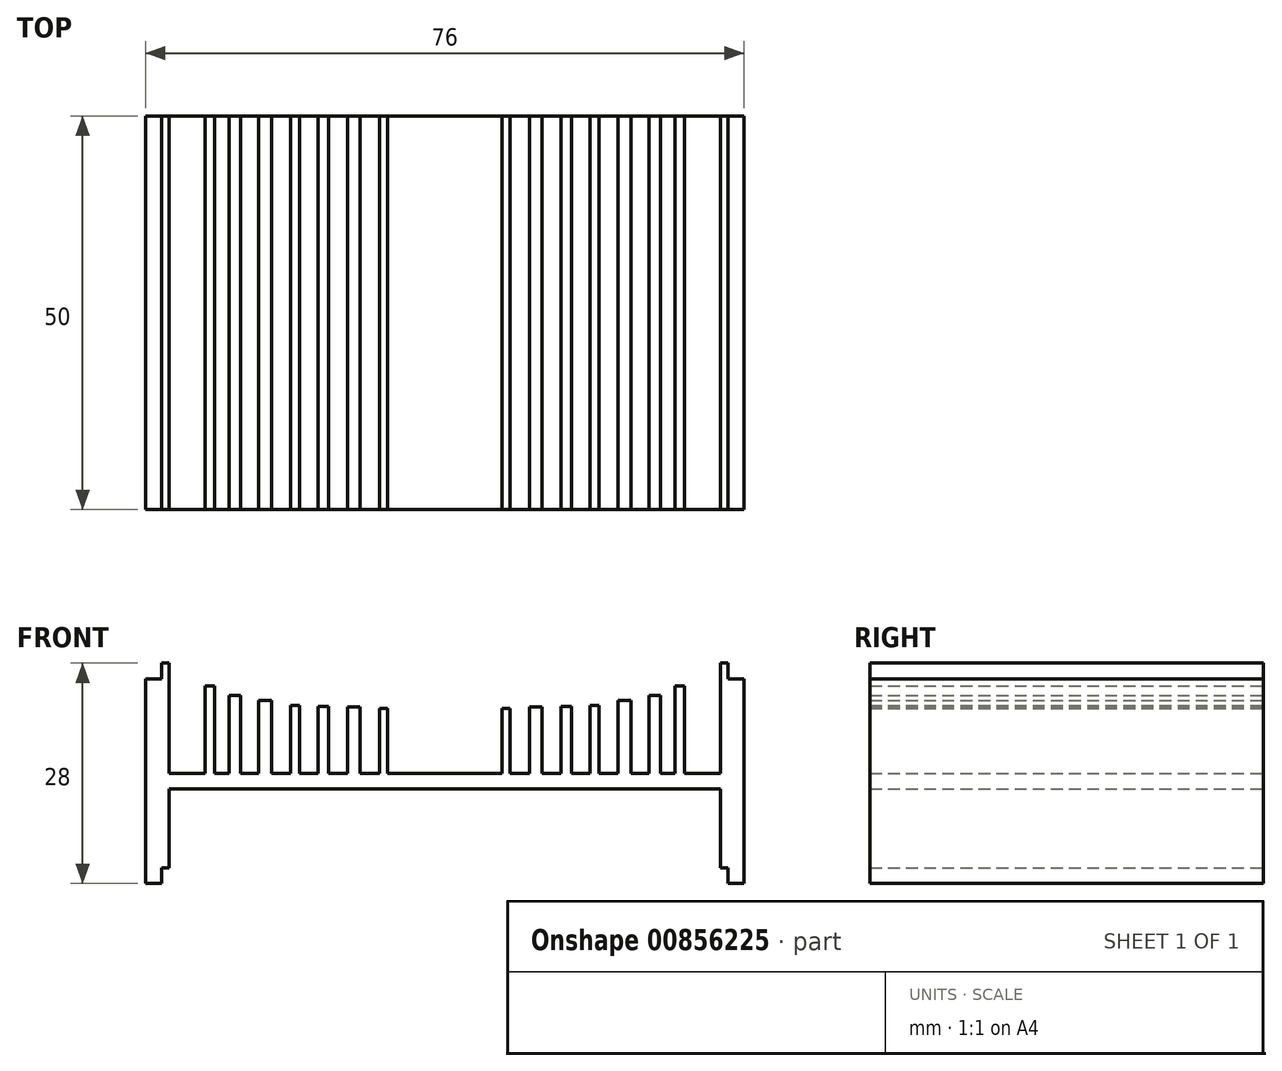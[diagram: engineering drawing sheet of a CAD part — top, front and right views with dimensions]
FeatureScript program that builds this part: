
annotation { "Feature Type Name" : "Feature", "Feature Type Description" : "" }
export const myFeature = defineFeature(function(context is Context, id is Id, definition is map)
    precondition{}
    {
        {
            var Q0;
            Q0=qCreatedBy(makeId("Front.planeOp"),FACE);
            var sketch = newSketch(context, id + "F0", { "sketchPlane" : qUnion([Q0])});
            skLineSegment(sketch, "E0", {"start": v(-34.72, -1.16) * mm, "end": v(-34.72, -27.16) * mm});
            skLineSegment(sketch, "E1", {"start": v(-34.72, -27.16) * mm, "end": v(-32.72, -27.16) * mm});
            skLineSegment(sketch, "E2", {"start": v(-32.72, -27.16) * mm, "end": v(-32.72, -25.16) * mm});
            skLineSegment(sketch, "E3", {"start": v(-32.72, -25.16) * mm, "end": v(-31.72, -25.16) * mm});
            skLineSegment(sketch, "E4", {"start": v(-31.72, -25.16) * mm, "end": v(-31.72, -15.16) * mm});
            skLineSegment(sketch, "E5", {"start": v(-31.72, -15.16) * mm, "end": v(3.28, -15.16) * mm});
            skLineSegment(sketch, "E6", {"start": v(-34.72, -1.16) * mm, "end": v(-32.72, -1.16) * mm});
            skLineSegment(sketch, "E7", {"start": v(-32.72, -1.16) * mm, "end": v(-32.72, 0.84) * mm});
            skLineSegment(sketch, "E8", {"start": v(-32.72, 0.84) * mm, "end": v(-31.72, 0.84) * mm});
            skLineSegment(sketch, "E9", {"start": v(-31.72, 0.84) * mm, "end": v(-31.72, -13.16) * mm});
            skLineSegment(sketch, "E10", {"start": v(-31.72, -13.16) * mm, "end": v(-27.2, -13.16) * mm});
            skLineSegment(sketch, "E11", {"start": v(3.28, -13.16) * mm, "end": v(3.28, -15.16) * mm});
            skLineSegment(sketch, "E12", {"start": v(3.28, 2.27) * mm, "end": v(3.28, -31.1) * mm, "construction": true});
            skLineSegment(sketch, "E13.MirrorCS", {"start": v(41.28, -1.16) * mm, "end": v(41.28, -27.16) * mm});
            skLineSegment(sketch, "E14.MirrorCS", {"start": v(38.28, 0.84) * mm, "end": v(38.28, -13.16) * mm});
            skLineSegment(sketch, "E15.MirrorCS", {"start": v(41.28, -1.16) * mm, "end": v(39.28, -1.16) * mm});
            skLineSegment(sketch, "E16.MirrorCS", {"start": v(39.28, -1.16) * mm, "end": v(39.28, 0.84) * mm});
            skLineSegment(sketch, "E17.MirrorCS", {"start": v(39.28, 0.84) * mm, "end": v(38.28, 0.84) * mm});
            skLineSegment(sketch, "E18.MirrorCS", {"start": v(38.28, -13.16) * mm, "end": v(33.75, -13.16) * mm});
            skLineSegment(sketch, "E19.MirrorCS", {"start": v(38.28, -15.16) * mm, "end": v(3.28, -15.16) * mm});
            skLineSegment(sketch, "E20.MirrorCS", {"start": v(38.28, -25.16) * mm, "end": v(38.28, -15.16) * mm});
            skLineSegment(sketch, "E21.MirrorCS", {"start": v(39.28, -25.16) * mm, "end": v(38.28, -25.16) * mm});
            skLineSegment(sketch, "E22.MirrorCS", {"start": v(41.28, -27.16) * mm, "end": v(39.28, -27.16) * mm});
            skLineSegment(sketch, "E23.MirrorCS", {"start": v(39.28, -27.16) * mm, "end": v(39.28, -25.16) * mm});
            skLineSegment(sketch, "E24", {"start": v(-27.2, -13.16) * mm, "end": v(-27.2, -2.1) * mm});
            skLineSegment(sketch, "E25", {"start": v(-27.2, -2.1) * mm, "end": v(-25.98, -2.1) * mm});
            skLineSegment(sketch, "E26", {"start": v(-25.98, -2.1) * mm, "end": v(-25.98, -13.16) * mm});
            skLineSegment(sketch, "E27.trimOffspring", {"start": v(-25.98, -13.16) * mm, "end": v(-24.09, -13.16) * mm});
            skLineSegment(sketch, "E28", {"start": v(-24.09, -13.16) * mm, "end": v(-24.09, -3.29) * mm});
            skLineSegment(sketch, "E29", {"start": v(-24.09, -3.29) * mm, "end": v(-22.68, -3.29) * mm});
            skLineSegment(sketch, "E30", {"start": v(-22.68, -3.29) * mm, "end": v(-22.68, -13.16) * mm});
            skLineSegment(sketch, "E31", {"start": v(-22.68, -13.16) * mm, "end": v(-20.35, -13.16) * mm});
            skLineSegment(sketch, "E32", {"start": v(-20.35, -13.16) * mm, "end": v(-20.35, -3.9) * mm});
            skLineSegment(sketch, "E33", {"start": v(-20.35, -3.9) * mm, "end": v(-18.7, -3.9) * mm});
            skLineSegment(sketch, "E34", {"start": v(-18.7, -3.9) * mm, "end": v(-18.7, -13.16) * mm});
            skLineSegment(sketch, "E35", {"start": v(-18.7, -13.16) * mm, "end": v(-16.3, -13.16) * mm});
            skLineSegment(sketch, "E36", {"start": v(-16.3, -13.16) * mm, "end": v(-16.3, -4.5) * mm});
            skLineSegment(sketch, "E37", {"start": v(-16.3, -4.5) * mm, "end": v(-15.14, -4.5) * mm});
            skLineSegment(sketch, "E38", {"start": v(-15.14, -4.5) * mm, "end": v(-15.14, -13.16) * mm});
            skLineSegment(sketch, "E39", {"start": v(-15.14, -13.16) * mm, "end": v(-12.81, -13.16) * mm});
            skLineSegment(sketch, "E40", {"start": v(-12.81, -13.16) * mm, "end": v(-12.81, -4.69) * mm});
            skLineSegment(sketch, "E41", {"start": v(-12.81, -4.69) * mm, "end": v(-11.47, -4.69) * mm});
            skLineSegment(sketch, "E42", {"start": v(-11.47, -4.69) * mm, "end": v(-11.47, -13.16) * mm});
            skLineSegment(sketch, "E43", {"start": v(-9.08, -13.16) * mm, "end": v(-9.08, -4.75) * mm});
            skLineSegment(sketch, "E44", {"start": v(-9.08, -4.75) * mm, "end": v(-7.48, -4.75) * mm});
            skLineSegment(sketch, "E45", {"start": v(-7.48, -4.75) * mm, "end": v(-7.48, -13.16) * mm});
            skLineSegment(sketch, "E46", {"start": v(-7.48, -13.16) * mm, "end": v(-5.03, -13.16) * mm});
            skLineSegment(sketch, "E47", {"start": v(-5.03, -13.16) * mm, "end": v(-5.03, -4.93) * mm});
            skLineSegment(sketch, "E48", {"start": v(-5.03, -4.93) * mm, "end": v(-4, -4.93) * mm});
            skLineSegment(sketch, "E49", {"start": v(-4, -4.93) * mm, "end": v(-4, -13.16) * mm});
            skLineSegment(sketch, "E50.trimOffspring", {"start": v(-4, -13.16) * mm, "end": v(3.28, -13.16) * mm});
            skLineSegment(sketch, "E51", {"start": v(-11.47, -13.16) * mm, "end": v(-9.08, -13.16) * mm});
            skLineSegment(sketch, "E52", {"start": v(-11.47, -13.16) * mm, "end": v(-11.47, -13.16) * mm});
            skLineSegment(sketch, "E53.MirrorCS", {"start": v(10.55, -4.93) * mm, "end": v(10.55, -13.16) * mm});
            skLineSegment(sketch, "E54.MirrorCS", {"start": v(11.6, -13.16) * mm, "end": v(11.6, -4.93) * mm});
            skLineSegment(sketch, "E55.MirrorCS", {"start": v(11.6, -4.93) * mm, "end": v(10.55, -4.93) * mm});
            skLineSegment(sketch, "E56.MirrorCS", {"start": v(19.37, -4.69) * mm, "end": v(18.03, -4.69) * mm});
            skLineSegment(sketch, "E57.MirrorCS", {"start": v(30.65, -3.29) * mm, "end": v(29.24, -3.29) * mm});
            skLineSegment(sketch, "E58.MirrorCS", {"start": v(22.87, -4.5) * mm, "end": v(21.7, -4.5) * mm});
            skLineSegment(sketch, "E59.MirrorCS", {"start": v(33.75, -2.1) * mm, "end": v(32.54, -2.1) * mm});
            skLineSegment(sketch, "E60.MirrorCS", {"start": v(26.91, -3.9) * mm, "end": v(25.26, -3.9) * mm});
            skLineSegment(sketch, "E61.MirrorCS", {"start": v(15.64, -4.75) * mm, "end": v(14.04, -4.75) * mm});
            skLineSegment(sketch, "E62.MirrorCS", {"start": v(21.7, -13.16) * mm, "end": v(19.37, -13.16) * mm});
            skLineSegment(sketch, "E63.MirrorCS", {"start": v(14.04, -13.16) * mm, "end": v(11.6, -13.16) * mm});
            skLineSegment(sketch, "E64.MirrorCS", {"start": v(29.24, -13.16) * mm, "end": v(26.91, -13.16) * mm});
            skLineSegment(sketch, "E65.MirrorCS", {"start": v(25.26, -13.16) * mm, "end": v(22.87, -13.16) * mm});
            skLineSegment(sketch, "E66.MirrorCS", {"start": v(26.91, -13.16) * mm, "end": v(26.91, -3.9) * mm});
            skLineSegment(sketch, "E67.MirrorCS", {"start": v(32.54, -2.1) * mm, "end": v(32.54, -13.16) * mm});
            skLineSegment(sketch, "E68.MirrorCS", {"start": v(30.65, -13.16) * mm, "end": v(30.65, -3.29) * mm});
            skLineSegment(sketch, "E69.MirrorCS", {"start": v(18.03, -4.69) * mm, "end": v(18.03, -13.16) * mm});
            skLineSegment(sketch, "E70.MirrorCS", {"start": v(19.37, -13.16) * mm, "end": v(19.37, -4.69) * mm});
            skLineSegment(sketch, "E71.MirrorCS", {"start": v(29.24, -3.29) * mm, "end": v(29.24, -13.16) * mm});
            skLineSegment(sketch, "E72.MirrorCS", {"start": v(22.87, -13.16) * mm, "end": v(22.87, -4.5) * mm});
            skLineSegment(sketch, "E73.MirrorCS", {"start": v(25.26, -3.9) * mm, "end": v(25.26, -13.16) * mm});
            skLineSegment(sketch, "E74.MirrorCS", {"start": v(15.64, -13.16) * mm, "end": v(15.64, -4.75) * mm});
            skLineSegment(sketch, "E75.MirrorCS", {"start": v(14.04, -4.75) * mm, "end": v(14.04, -13.16) * mm});
            skLineSegment(sketch, "E76.MirrorCS", {"start": v(33.75, -13.16) * mm, "end": v(33.75, -2.1) * mm});
            skLineSegment(sketch, "E77.MirrorCS", {"start": v(18.03, -13.16) * mm, "end": v(18.03, -13.16) * mm});
            skLineSegment(sketch, "E78.MirrorCS", {"start": v(32.54, -13.16) * mm, "end": v(30.65, -13.16) * mm});
            skLineSegment(sketch, "E79.MirrorCS", {"start": v(18.03, -13.16) * mm, "end": v(15.64, -13.16) * mm});
            skLineSegment(sketch, "E80.MirrorCS", {"start": v(21.7, -4.5) * mm, "end": v(21.7, -13.16) * mm});
            skLineSegment(sketch, "E81.trimOffspring", {"start": v(10.55, -13.16) * mm, "end": v(3.28, -13.16) * mm});
            skSolve(sketch);
        }
        {
            var Q0;
            Q0 = qSketchRegion(id + "F0", true);
            extrude(context, id + "F1", {"entities" : qUnion([Q0]), "depth" : 50 * mm, "offsetDistance" : 25 * mm});
        }
    });
